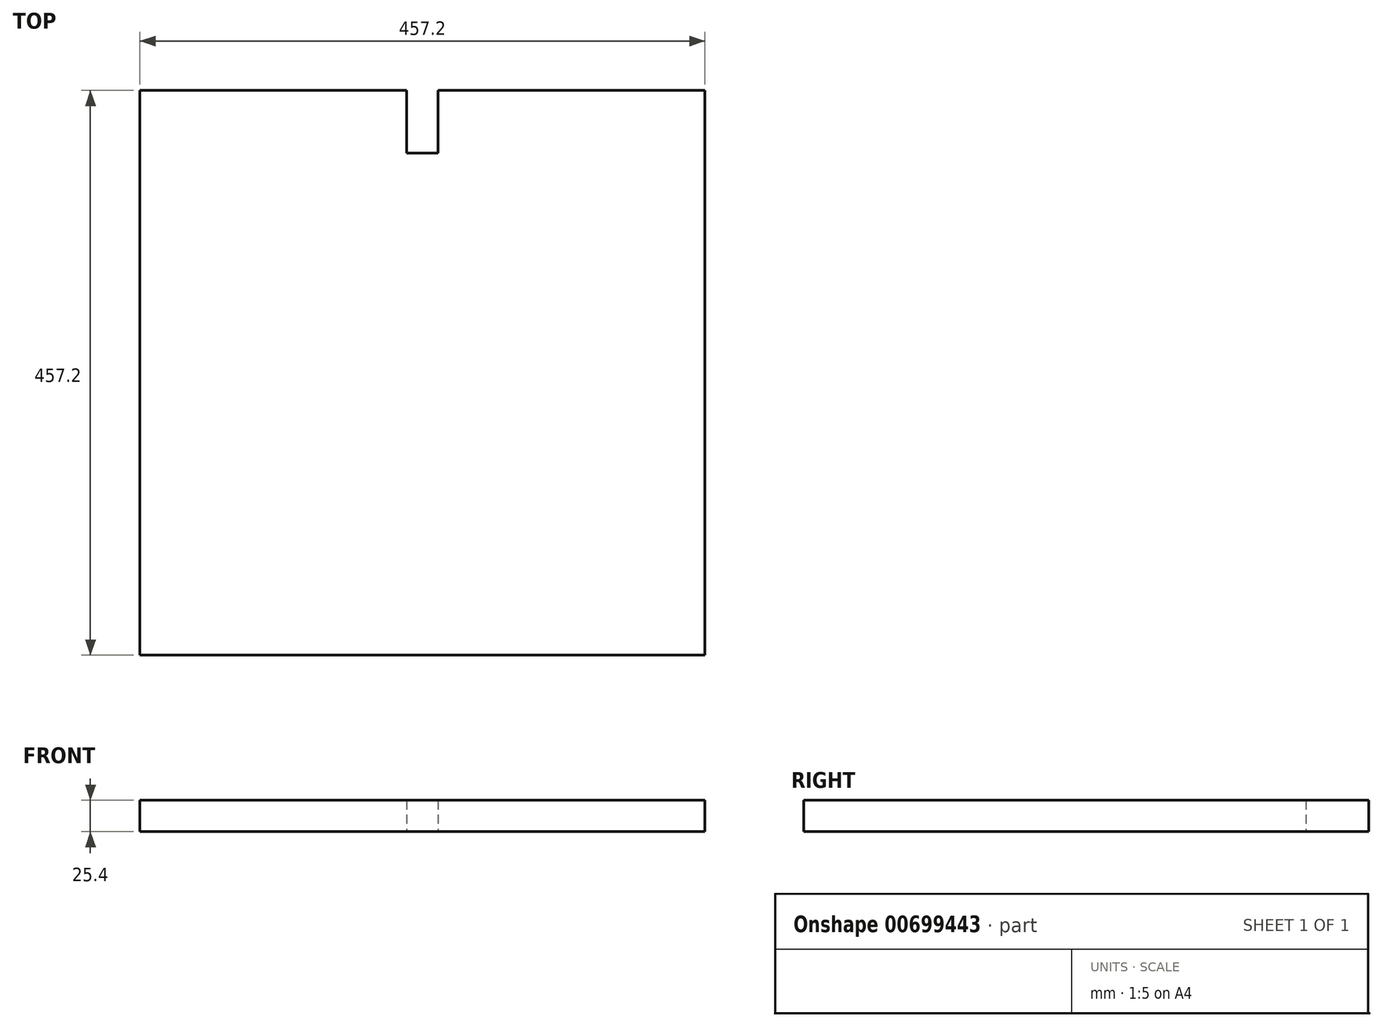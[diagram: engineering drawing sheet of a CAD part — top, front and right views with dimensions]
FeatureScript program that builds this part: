
annotation { "Feature Type Name" : "Feature", "Feature Type Description" : "" }
export const myFeature = defineFeature(function(context is Context, id is Id, definition is map)
    precondition{}
    {
        {
            var Q0;
            Q0=qCreatedBy(makeId("Top.planeOp"),FACE);
            var sketch = newSketch(context, id + "F0", { "sketchPlane" : qUnion([Q0])});
            skLineSegment(sketch, "E0", {"start": v(0, 0) * mm, "end": v(0, 457.2) * mm});
            skLineSegment(sketch, "E1", {"start": v(0, 457.2) * mm, "end": v(241.3, 457.2) * mm});
            skLineSegment(sketch, "E2", {"start": v(241.3, 457.2) * mm, "end": v(241.3, 406.4) * mm});
            skLineSegment(sketch, "E3", {"start": v(215.9, 406.4) * mm, "end": v(241.3, 406.4) * mm});
            skLineSegment(sketch, "E4", {"start": v(215.9, 406.4) * mm, "end": v(215.9, 457.2) * mm});
            skLineSegment(sketch, "E5", {"start": v(215.9, 457.2) * mm, "end": v(457.2, 457.2) * mm});
            skLineSegment(sketch, "E6", {"start": v(457.2, 457.2) * mm, "end": v(457.2, 0) * mm});
            skLineSegment(sketch, "E7", {"start": v(457.2, 0) * mm, "end": v(0, 0) * mm});
            skSolve(sketch);
        }
        {
            var Q0;
            Q0=makeQuery(id+"F0.imprint","IMPRINT",FACE,{"disambiguationData":[TD([[makeQuery(id+"F0.imprint","IMPRINT",EDGE,{"derivedFrom":sQuery(id+"F0.wireOp",EDGE,"E0")}),-1.0]])]});
            extrude(context, id + "F1", {"entities" : qUnion([Q0]), "depth" : 25.4 * mm, "offsetDistance" : 25.4 * mm});
        }
    });
